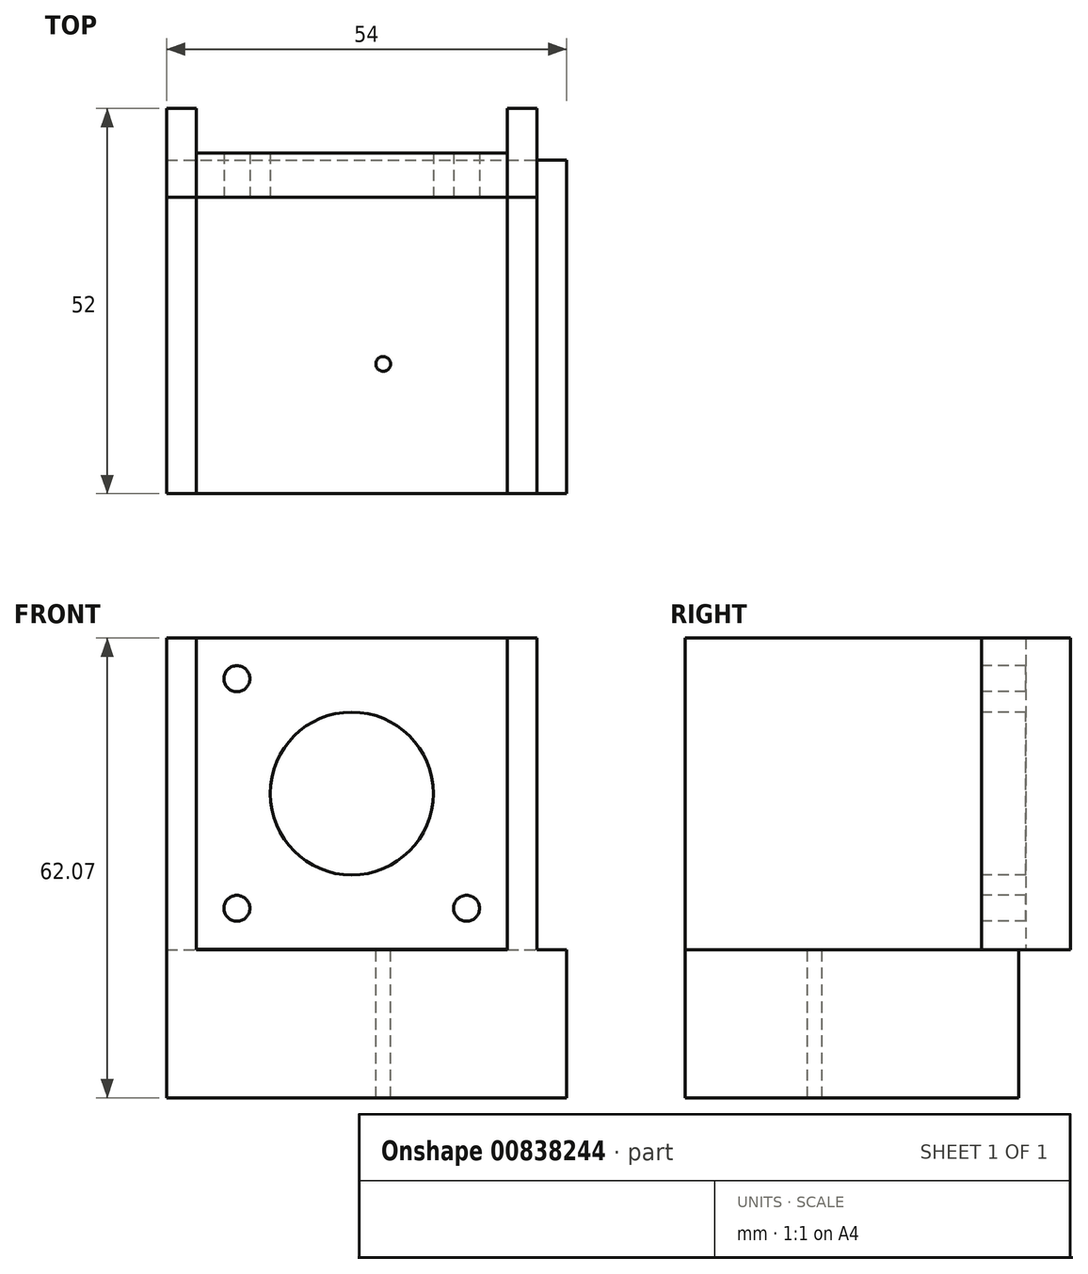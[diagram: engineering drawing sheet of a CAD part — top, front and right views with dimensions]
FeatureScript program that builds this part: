
annotation { "Feature Type Name" : "Feature", "Feature Type Description" : "" }
export const myFeature = defineFeature(function(context is Context, id is Id, definition is map)
    precondition{}
    {
        {
            var Q0;
            Q0=qCreatedBy(makeId("Front.planeOp"),FACE);
            var sketch = newSketch(context, id + "F0", { "sketchPlane" : qUnion([Q0])});
            skLineSegment(sketch, "E0.bottom", {"start": v(-15.5, 15.5) * mm, "end": v(15.5, 15.5) * mm});
            skLineSegment(sketch, "E0.top", {"start": v(-15.5, -15.5) * mm, "end": v(15.5, -15.5) * mm});
            skLineSegment(sketch, "E0.left", {"start": v(-15.5, 15.5) * mm, "end": v(-15.5, -15.5) * mm});
            skLineSegment(sketch, "E0.right", {"start": v(15.5, 15.5) * mm, "end": v(15.5, -15.5) * mm});
            skPoint(sketch, "E0.middle", {"position": v(0, 0) * mm});
            skLineSegment(sketch, "E1.bottom", {"start": v(-21, 21) * mm, "end": v(21, 21) * mm});
            skLineSegment(sketch, "E1.top", {"start": v(-21, -21) * mm, "end": v(21, -21) * mm});
            skLineSegment(sketch, "E1.left", {"start": v(-21, 21) * mm, "end": v(-21, -21) * mm});
            skLineSegment(sketch, "E1.right", {"start": v(21, 21) * mm, "end": v(21, -21) * mm});
            skCircle(sketch, "E2", {"center": v(-15.5, 15.5) * mm, "radius": 1.75 * mm});
            skCircle(sketch, "E3", {"center": v(-15.5, -15.5) * mm, "radius": 1.75 * mm});
            skCircle(sketch, "E4", {"center": v(15.5, -15.5) * mm, "radius": 1.75 * mm});
            skCircle(sketch, "E5", {"center": v(0, 0) * mm, "radius": 11 * mm});
            skLineSegment(sketch, "E6.bottom", {"start": v(-25, -21.07) * mm, "end": v(29, -21.07) * mm});
            skLineSegment(sketch, "E6.top", {"start": v(-25, -41.07) * mm, "end": v(29, -41.07) * mm});
            skLineSegment(sketch, "E6.left", {"start": v(-25, -21.07) * mm, "end": v(-25, -41.07) * mm});
            skLineSegment(sketch, "E6.right", {"start": v(29, -21.07) * mm, "end": v(29, -41.07) * mm});
            skLineSegment(sketch, "E7.bottom", {"start": v(-21, 21) * mm, "end": v(-25, 21) * mm});
            skLineSegment(sketch, "E7.top", {"start": v(-21, -41.07) * mm, "end": v(-25, -41.07) * mm});
            skLineSegment(sketch, "E7.left", {"start": v(-21, 21) * mm, "end": v(-21, -41.07) * mm});
            skLineSegment(sketch, "E7.right", {"start": v(-25, 21) * mm, "end": v(-25, -41.07) * mm});
            skLineSegment(sketch, "E8.bottom", {"start": v(21, 21) * mm, "end": v(25, 21) * mm});
            skLineSegment(sketch, "E8.top", {"start": v(21, -41.07) * mm, "end": v(25, -41.07) * mm});
            skLineSegment(sketch, "E8.left", {"start": v(21, 21) * mm, "end": v(21, -41.07) * mm});
            skLineSegment(sketch, "E8.right", {"start": v(25, 21) * mm, "end": v(25, -41.07) * mm});
            skSolve(sketch);
        }
        {
            var Q0;
            Q0=makeQuery(id+"F0.imprint","IMPRINT",FACE,{"disambiguationData":[TD([[makeQuery(id+"F0.imprint","IMPRINT",EDGE,{"derivedFrom":sQuery(id+"F0.wireOp",EDGE,"E1.bottom")}),-1.0]])]});
            var Q1;
            Q1=makeQuery(id+"F0.imprint","IMPRINT",FACE,{"disambiguationData":[TD([[makeQuery(id+"F0.imprint","IMPRINT",EDGE,{"derivedFrom":sQuery(id+"F0.wireOp",EDGE,"E5")}),-1.0]])]});
            extrude(context, id + "F1", {"entities" : qUnion([Q0, Q1]), "oppositeDirection" : true, "depth" : 6 * mm, "offsetDistance" : 25 * mm});
        }
        {
            var Q0;
            Q0=makeQuery(id+"F0.imprint","IMPRINT",FACE,{"disambiguationData":[TD([[makeQuery(id+"F0.imprint","IMPRINT",EDGE,{"derivedFrom":sQuery(id+"F0.wireOp",EDGE,"E6.bottom")}),-1.0]])]});
            extrude(context, id + "F2", {"entities" : qUnion([Q0]), "depth" : 40 * mm, "offsetDistance" : 25 * mm});
        }
        {
            var Q0;
            Q0=makeQuery(id+"F2.opExtrude","CAP_FACE",FACE,{"disambiguationData":[OSD([sQuery(id+"F0.wireOp",EDGE,"E6.bottom"),sQuery(id+"F0.wireOp",EDGE,"E6.top"),sQuery(id+"F0.wireOp",EDGE,"E6.left"),sQuery(id+"F0.wireOp",EDGE,"E6.right")])],"isStart":true});
            extrude(context, id + "F3", {"entities" : qUnion([Q0]), "operationType" : NewBodyOperationType.ADD, "depth" : 5 * mm, "offsetDistance" : 25 * mm});
        }
        {
            var Q0;
            {var subQ1=sQuery(id+"F0.wireOp",EDGE,"E7.bottom");Q0=makeQuery(id+"F0.imprint","IMPRINT",FACE,{"disambiguationData":[TD([[makeQuery(id+"F0.imprint","IMPRINT",EDGE,{"derivedFrom":subQ1}),1.0]])]});}
            var Q1;
            {var subQ5=sQuery(id+"F0.wireOp",EDGE,"E7.top");Q1=makeQuery(id+"F0.imprint","IMPRINT",FACE,{"disambiguationData":[TD([[makeQuery(id+"F0.imprint","IMPRINT",EDGE,{"derivedFrom":subQ5}),-1.0]])]});}
            var Q2;
            {var subQ1=sQuery(id+"F0.wireOp",EDGE,"E8.bottom");Q2=makeQuery(id+"F0.imprint","IMPRINT",FACE,{"disambiguationData":[TD([[makeQuery(id+"F0.imprint","IMPRINT",EDGE,{"derivedFrom":subQ1}),-1.0]])]});}
            var Q3;
            {var subQ5=sQuery(id+"F0.wireOp",EDGE,"E8.top");Q3=makeQuery(id+"F0.imprint","IMPRINT",FACE,{"disambiguationData":[TD([[makeQuery(id+"F0.imprint","IMPRINT",EDGE,{"derivedFrom":subQ5}),1.0]])]});}
            extrude(context, id + "F4", {"entities" : qUnion([Q0, Q1, Q2, Q3]), "depth" : 40 * mm, "offsetDistance" : 25 * mm});
        }
        {
            var Q0;
            Q0=makeQuery(id+"F4.opExtrude","SWEPT_BODY",BODY,{"disambiguationData":[OSD([sQuery(id+"F0.wireOp",EDGE,"E8.bottom"),sQuery(id+"F0.wireOp",EDGE,"E8.top"),sQuery(id+"F0.wireOp",EDGE,"E8.left"),sQuery(id+"F0.wireOp",EDGE,"E8.right")])]});
            var Q1;
            Q1=makeQuery(id+"F1.opExtrude","SWEPT_BODY",BODY,{"disambiguationData":[OSD([sQuery(id+"F0.wireOp",EDGE,"E1.bottom"),sQuery(id+"F0.wireOp",EDGE,"E2"),sQuery(id+"F0.wireOp",EDGE,"E3"),sQuery(id+"F0.wireOp",EDGE,"E4"),sQuery(id+"F0.wireOp",EDGE,"E5"),sQuery(id+"F0.wireOp",EDGE,"E1.top"),sQuery(id+"F0.wireOp",EDGE,"E7.left"),sQuery(id+"F0.wireOp",EDGE,"E8.left")])]});
            var Q2;
            Q2=makeQuery(id+"F4.opExtrude","SWEPT_BODY",BODY,{"disambiguationData":[OSD([sQuery(id+"F0.wireOp",EDGE,"E7.bottom"),sQuery(id+"F0.wireOp",EDGE,"E7.top"),sQuery(id+"F0.wireOp",EDGE,"E7.left"),sQuery(id+"F0.wireOp",EDGE,"E7.right")])]});
            var Q3;
            Q3=makeQuery(id+"F2.opExtrude","SWEPT_BODY",BODY,{"disambiguationData":[OSD([sQuery(id+"F0.wireOp",EDGE,"E6.bottom"),sQuery(id+"F0.wireOp",EDGE,"E6.top"),sQuery(id+"F0.wireOp",EDGE,"E6.right"),sQuery(id+"F0.wireOp",EDGE,"E7.top"),sQuery(id+"F0.wireOp",EDGE,"E7.right"),sQuery(id+"F0.wireOp",EDGE,"E8.top")])]});
            booleanBodies(context, id + "F5", {"operationType" : BooleanOperationType.UNION, "tools" : qUnion([Q0, Q1, Q2, Q3])});
        }
        {
            var Q0;
            {var subQ0=sQuery(id+"F0.wireOp",EDGE,"E6.bottom");Q0=makeQuery(id+"F3.boolean.opBoolean","MERGE",FACE,{"derivedFrom":[makeQuery(id+"F2.opExtrude","SWEPT_FACE",FACE,{"disambiguationData":[OSD([subQ0])]}),makeQuery(id+"F3.opExtrude","SWEPT_FACE",FACE,{"disambiguationData":[OSD([subQ0])]})]});}
            var sketch = newSketch(context, id + "F6", { "sketchPlane" : qUnion([Q0])});
            skLineSegment(sketch, "E9.bottom", {"start": v(-21, 0) * mm, "end": v(21, 0) * mm});
            skLineSegment(sketch, "E9.top", {"start": v(-21, -33) * mm, "end": v(21, -33) * mm});
            skLineSegment(sketch, "E9.left", {"start": v(-21, 0) * mm, "end": v(-21, -33) * mm});
            skLineSegment(sketch, "E9.right", {"start": v(21, 0) * mm, "end": v(21, -33) * mm});
            skCircle(sketch, "E10", {"center": v(4.25, -22.5) * mm, "radius": 1 * mm});
            skSolve(sketch);
        }
        {
            var Q0;
            Q0=makeQuery(id+"F6.imprint","IMPRINT",FACE,{"disambiguationData":[TD([[makeQuery(id+"F6.imprint","IMPRINT",EDGE,{"derivedFrom":sQuery(id+"F6.wireOp",EDGE,"E10")}),1.0]])]});
            extrude(context, id + "F7", {"entities" : qUnion([Q0]), "operationType" : NewBodyOperationType.REMOVE, "oppositeDirection" : true, "depth" : 25 * mm, "offsetDistance" : 25 * mm});
        }
        {
            var Q0;
            Q0=makeQuery(id+"F4.opExtrude","CAP_FACE",FACE,{"disambiguationData":[OSD([sQuery(id+"F0.wireOp",EDGE,"E8.bottom"),sQuery(id+"F0.wireOp",EDGE,"E8.top"),sQuery(id+"F0.wireOp",EDGE,"E8.left"),sQuery(id+"F0.wireOp",EDGE,"E8.right")])],"isStart":true});
            var Q1;
            Q1=makeQuery(id+"F4.opExtrude","CAP_FACE",FACE,{"disambiguationData":[OSD([sQuery(id+"F0.wireOp",EDGE,"E7.bottom"),sQuery(id+"F0.wireOp",EDGE,"E7.top"),sQuery(id+"F0.wireOp",EDGE,"E7.left"),sQuery(id+"F0.wireOp",EDGE,"E7.right")])],"isStart":true});
            extrude(context, id + "F8", {"entities" : qUnion([Q0, Q1]), "depth" : 12 * mm, "offsetDistance" : 25 * mm});
        }
    });
